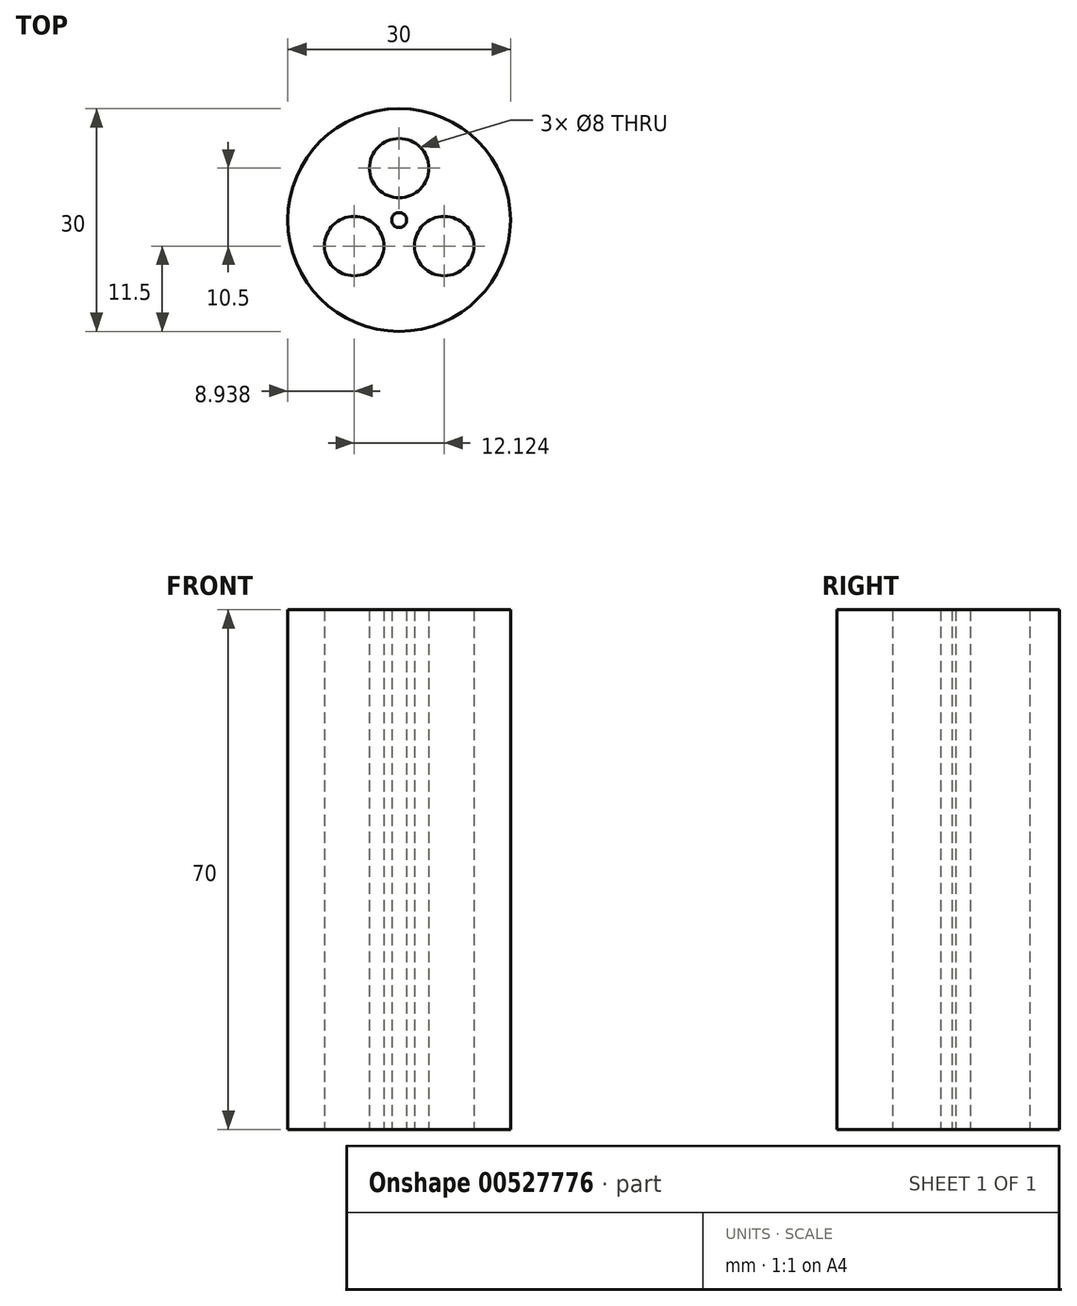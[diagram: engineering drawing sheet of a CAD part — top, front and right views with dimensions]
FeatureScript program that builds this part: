
annotation { "Feature Type Name" : "Feature", "Feature Type Description" : "" }
export const myFeature = defineFeature(function(context is Context, id is Id, definition is map)
    precondition{}
    {
        {
            var Q0;
            Q0=qCreatedBy(makeId("Top.planeOp"),FACE);
            var sketch = newSketch(context, id + "F0", { "sketchPlane" : qUnion([Q0])});
            skCircle(sketch, "E0", {"center": v(0, 0) * mm, "radius": 15 * mm});
            skCircle(sketch, "E1", {"center": v(-6.06, -3.5) * mm, "radius": 4 * mm});
            skCircle(sketch, "E2", {"center": v(0, 7) * mm, "radius": 4 * mm});
            skCircle(sketch, "E3", {"center": v(6.06, -3.5) * mm, "radius": 4 * mm});
            skCircle(sketch, "E4", {"center": v(0, 0) * mm, "radius": 1 * mm});
            skLineSegment(sketch, "E5", {"start": v(-6.06, -3.5) * mm, "end": v(0, 0) * mm, "construction": true});
            skLineSegment(sketch, "E6", {"start": v(0, 7) * mm, "end": v(0, 0) * mm, "construction": true});
            skLineSegment(sketch, "E7", {"start": v(6.06, -3.5) * mm, "end": v(0, 0) * mm, "construction": true});
            skLineSegment(sketch, "E8", {"start": v(6.06, -3.5) * mm, "end": v(0, 7) * mm, "construction": true});
            skSolve(sketch);
        }
        {
            var Q0;
            Q0 = qSketchRegion(id + "F0", true);
            extrude(context, id + "F1", {"entities" : qUnion([Q0]), "depth" : 70 * mm, "offsetDistance" : 25 * mm});
        }
    });
